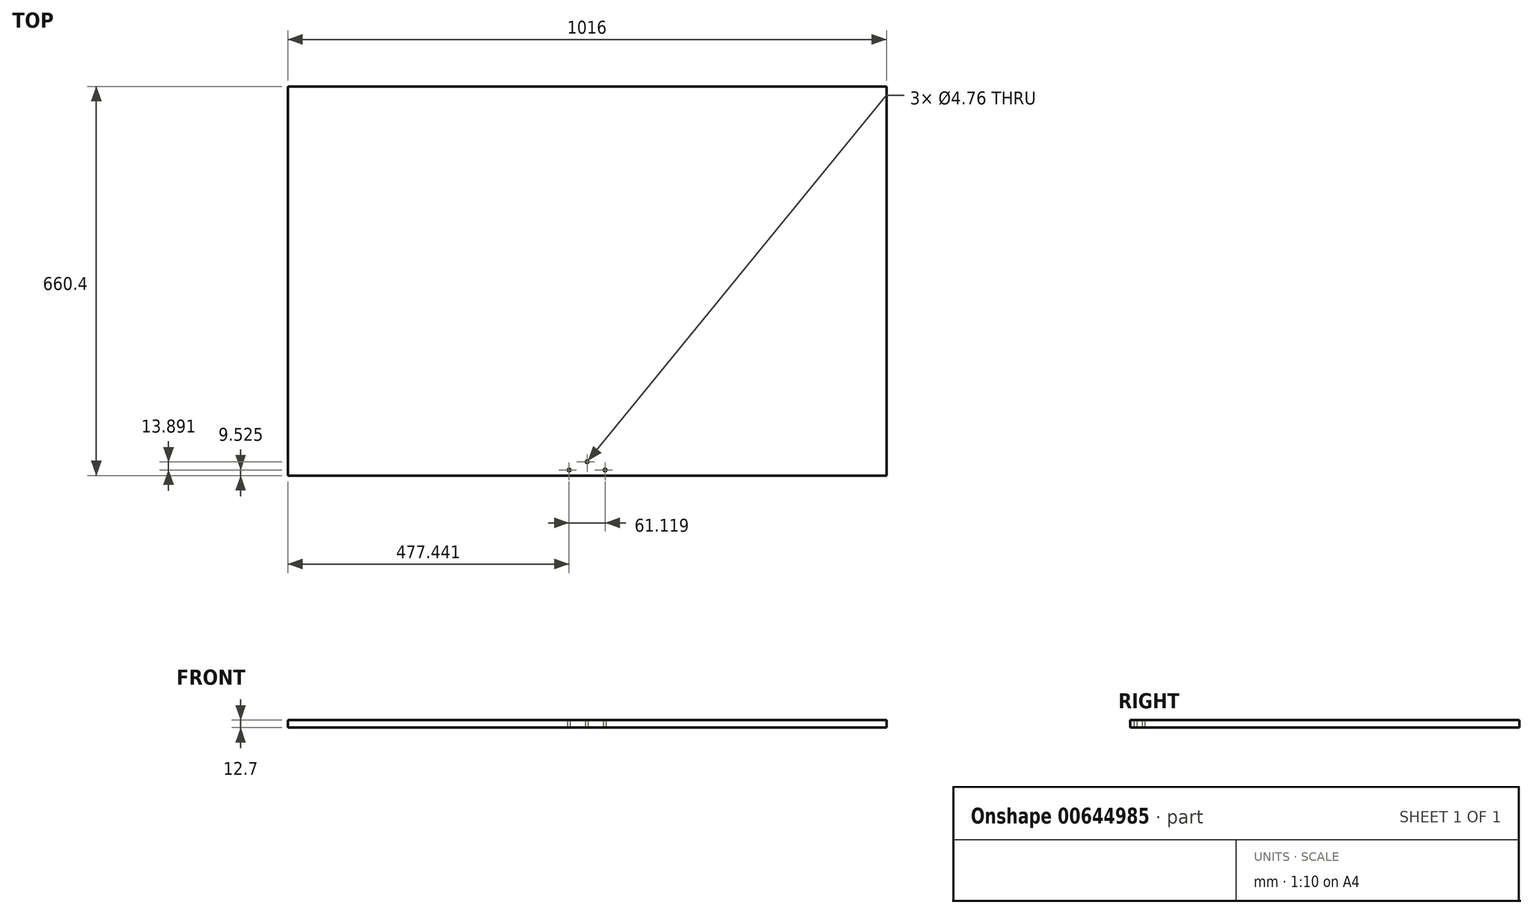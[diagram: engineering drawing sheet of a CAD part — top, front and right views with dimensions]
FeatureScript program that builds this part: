
annotation { "Feature Type Name" : "Feature", "Feature Type Description" : "" }
export const myFeature = defineFeature(function(context is Context, id is Id, definition is map)
    precondition{}
    {
        {
            var Q0;
            Q0=qCreatedBy(makeId("Top.planeOp"),FACE);
            var sketch = newSketch(context, id + "F0", { "sketchPlane" : qUnion([Q0])});
            skLineSegment(sketch, "E0.bottom", {"start": v(508, 330.2) * mm, "end": v(-508, 330.2) * mm});
            skLineSegment(sketch, "E0.top", {"start": v(508, -330.2) * mm, "end": v(-508, -330.2) * mm});
            skLineSegment(sketch, "E0.left", {"start": v(508, 330.2) * mm, "end": v(508, -330.2) * mm});
            skLineSegment(sketch, "E0.right", {"start": v(-508, 330.2) * mm, "end": v(-508, -330.2) * mm});
            skPoint(sketch, "E0.middle", {"position": v(0, 0) * mm});
            skSolve(sketch);
        }
        {
            var Q0;
            Q0=makeQuery(id+"F0.imprint","IMPRINT",FACE,{"disambiguationData":[TD([[makeQuery(id+"F0.imprint","IMPRINT",EDGE,{"derivedFrom":sQuery(id+"F0.wireOp",EDGE,"E0.bottom")}),1.0]])]});
            extrude(context, id + "F1", {"entities" : qUnion([Q0]), "depth" : 12.7 * mm, "offsetDistance" : 25.4 * mm});
        }
        {
            var Q0;
            Q0=makeQuery(id+"F1.opExtrude","CAP_FACE",FACE,{"disambiguationData":[OSD([sQuery(id+"F0.wireOp",EDGE,"E0.bottom"),sQuery(id+"F0.wireOp",EDGE,"E0.top"),sQuery(id+"F0.wireOp",EDGE,"E0.left"),sQuery(id+"F0.wireOp",EDGE,"E0.right")])],"isStart":false});
            var sketch = newSketch(context, id + "F2", { "sketchPlane" : qUnion([Q0])});
            skLineSegment(sketch, "E1.bottom", {"start": v(-508, -330.2) * mm, "end": v(0, -330.2) * mm});
            skLineSegment(sketch, "E1.top", {"start": v(-508, -323.85) * mm, "end": v(0, -323.85) * mm});
            skLineSegment(sketch, "E1.left", {"start": v(-508, -330.2) * mm, "end": v(-508, -323.85) * mm});
            skLineSegment(sketch, "E1.right", {"start": v(0, -330.2) * mm, "end": v(0, -323.85) * mm});
            skLineSegment(sketch, "E2.bottom", {"start": v(30.56, -320.68) * mm, "end": v(-30.56, -320.68) * mm});
            skLineSegment(sketch, "E2.top", {"start": v(30.56, -327.03) * mm, "end": v(-30.56, -327.03) * mm});
            skLineSegment(sketch, "E2.left", {"start": v(30.56, -320.68) * mm, "end": v(30.56, -327.03) * mm});
            skLineSegment(sketch, "E2.right", {"start": v(-30.56, -320.68) * mm, "end": v(-30.56, -327.03) * mm});
            skPoint(sketch, "E2.middle", {"position": v(0, -323.85) * mm});
            skCircle(sketch, "E3", {"center": v(-30.56, -320.68) * mm, "radius": 2.38 * mm});
            skCircle(sketch, "E4", {"center": v(30.56, -320.68) * mm, "radius": 2.38 * mm});
            skLineSegment(sketch, "E5", {"start": v(-30.56, -320.68) * mm, "end": v(-30.56, -306.78) * mm});
            skLineSegment(sketch, "E6", {"start": v(-30.56, -306.78) * mm, "end": v(0, -306.78) * mm});
            skCircle(sketch, "E7", {"center": v(0, -306.78) * mm, "radius": 2.38 * mm});
            skSolve(sketch);
        }
        {
            var Q0;
            Q0=makeQuery(id+"F2.imprint","IMPRINT",FACE,{"disambiguationData":[TD([[makeQuery(id+"F2.imprint","IMPRINT",EDGE,{"derivedFrom":sQuery(id+"F2.wireOp",EDGE,"E7")}),1.0]])]});
            var Q1;
            {var subQ0=sQuery(id+"F2.wireOp",EDGE,"E2.left");var subQ1=sQuery(id+"F2.wireOp",EDGE,"E2.bottom");var subQ2=makeQuery(id+"F2.imprint","INTERSECT",VERTEX,{"derivedFrom":[subQ1,subQ0]});Q1=makeQuery(id+"F2.imprint","IMPRINT",FACE,{"disambiguationData":[TD([[makeQuery(id+"F2.imprint","IMPRINT",EDGE,{"disambiguationData":[TD([[subQ2,-1.0]])],"derivedFrom":subQ1}),1.0]])]});}
            var Q2;
            {var subQ0=sQuery(id+"F2.wireOp",EDGE,"E2.left");var subQ1=sQuery(id+"F2.wireOp",EDGE,"E2.bottom");var subQ2=makeQuery(id+"F2.imprint","INTERSECT",VERTEX,{"derivedFrom":[subQ1,subQ0]});Q2=makeQuery(id+"F2.imprint","IMPRINT",FACE,{"disambiguationData":[TD([[makeQuery(id+"F2.imprint","IMPRINT",EDGE,{"disambiguationData":[TD([[subQ2,-1.0]])],"derivedFrom":subQ1}),-1.0]])]});}
            var Q3;
            {var subQ1=sQuery(id+"F2.wireOp",EDGE,"E2.bottom");var subQ3=sQuery(id+"F2.wireOp",EDGE,"E3");var subQ4=makeQuery(id+"F2.imprint","INTERSECT",VERTEX,{"derivedFrom":[subQ1,subQ3]});Q3=makeQuery(id+"F2.imprint","IMPRINT",FACE,{"disambiguationData":[TD([[makeQuery(id+"F2.imprint","IMPRINT",EDGE,{"disambiguationData":[TD([[subQ4,1.0]])],"derivedFrom":subQ3}),1.0]])]});}
            var Q4;
            {var subQ0=sQuery(id+"F2.wireOp",EDGE,"E5");var subQ3=sQuery(id+"F2.wireOp",EDGE,"E3");var subQ5=makeQuery(id+"F2.imprint","INTERSECT",VERTEX,{"derivedFrom":[subQ3,subQ0]});Q4=makeQuery(id+"F2.imprint","IMPRINT",FACE,{"disambiguationData":[TD([[makeQuery(id+"F2.imprint","IMPRINT",EDGE,{"disambiguationData":[TD([[subQ5,1.0]])],"derivedFrom":subQ3}),1.0]])]});}
            var Q5;
            {var subQ0=sQuery(id+"F2.wireOp",EDGE,"E5");var subQ3=sQuery(id+"F2.wireOp",EDGE,"E3");var subQ5=makeQuery(id+"F2.imprint","INTERSECT",VERTEX,{"derivedFrom":[subQ3,subQ0]});Q5=makeQuery(id+"F2.imprint","IMPRINT",FACE,{"disambiguationData":[TD([[makeQuery(id+"F2.imprint","IMPRINT",EDGE,{"disambiguationData":[TD([[subQ5,-1.0]])],"derivedFrom":subQ3}),1.0]])]});}
            extrude(context, id + "F3", {"entities" : qUnion([Q0, Q1, Q2, Q3, Q4, Q5]), "operationType" : NewBodyOperationType.REMOVE, "oppositeDirection" : true, "depth" : 25.4 * mm, "offsetDistance" : 25.4 * mm});
        }
    });
